# Revit family: 6MLH-NRG
name_source: partatom
category: Mechanical Equipment
revit_build: Autodesk Revit 2017 (Build: 20190508_0315(x64)
units: mm (PartAtom-declared; Revit-internal decimal feet)

## family parameters
Always vertical = Yes
Cut with Voids When Loaded = No
OmniClass Number = 23.40.40.11.17
OmniClass Title = Refrigerated Cases
Part Type = Normal
Room Calculation Point = No
Round Connector Dimension = Use Radius
Shared = No
Work Plane-Based = Yes

## types (12) — shared parameters
24" Shelf = Yes
BOTTOM ELECTRICAL = Yes
BOTTOM REFRIGERATION PIPING = Yes
Certifications = NSF 7, UL471, CSA
DATE = 04/29/2016
DRAIN PIPING = Yes
Default Elevation = 48"
Description = High Multi-Deck Merchandiser with Synerg-E™
Discharge Air Velocity (FPM) = 260 FPM
EQUIPMENT DESCRIPTION = High Multi-Deck Merchandiser with Synerg-E™
EQUIPMENT MARK = 6MLH-NRG
GLASS = Glass
Height = 88 5/8"
Item Description = High Multi-Deck Merchandiser with Synerg-E™
LF STD END = Yes
Legend Number = 6MLH-NRG
Manufacturer = HILL PHOENIX
Model = 6MLH-NRG
PAINTED METAL UPPER SHELF = PAINTED SHELVES
REFRIGERATION PIPING = COPPER PIPE
RT STD END = Yes
STAINLESS STEEL = GALVANIZED STEEL
Standard Power Amps = 0 A
Superheat Set Point @ Bulb (°F) = 6-8 °F
TOP ELECTRICAL = Yes
TOP REFRIGERATION PIPING = Yes
URL = http://www.hillphoenix.com
Width = 42 3/4"

## per-type parameters (varying)
| type | Application Discipline | BTUH Conventional | BTUH Parallel | DRAIN LINE | Defrosts Per Day | Discharge Air (°F) | ENDS 4 SECTION | Evaporator (°F) | High Efficiency Amps | High Efficiency Watts | High Power (Cornice) Amps | High Power (Cornice) Watts | Length | Length of Cases | Light Length | Lights Per Row | Number of Fans | Standard Power Watts | Timed-Off Defrost Fail-Safe (Min) | Timed-Off Defrost Termination Temp |
| 04' Dairy/Deli/Cut Produce | Fresh Meat | 1915 | 1770 | 24" | 2 | 30 °F | Yes | 27 °F | 1 A | 65 W | 1 A | 65 W | 48" | 48" | 3' | 2 | 3 | 36 W | 30 (min) | 42 °F |
| 06' Dairy/Deli/Cut Produce | Dairy/Deli/Cut Produce | 1756 | 1500 | 36" | 6 | 34 °F | Yes | 25 °F | 1 A | 65 W | 0 A | 30 W | 72" | 72" | 3' | 2 | 3 | 17 W | 45 (min) | 42 °F |
| 08' Dairy/Deli/Cut Produce | Dairy/Deli/Cut Produce | 1756 | 1500 | 48" | 8 | 34 °F | Yes | 25 °F | 1 A | 65 W | 0 A | 43 W | 96" | 96" | 4' | 2 | 3 | 24 W | 45 | 45 °F |
| 12' Dairy/Deli/Cut Produce | Dairy/Deli/Cut Produce | 1756 | 1500 | 72" | 6 | 34 °F | Yes | 25 °F | 1 A | 87 W | 1 A | 65 W | 144" | 144" | 4' | 3 | 4 | 36 W | 45 (min) | 42 °F |
| 04' Bulk Produce/Beverage | Bulk Produce/Beverage | 1545 | 1475 | 24" | 6 | 37 °F | No | 34 °F | 0 A | 43 W | 0 A | 22 W | 48" | 48" | 4' | 1 | 2 | 12 W | 45 (min) | 42 °F |
| 06' Bulk Produce/Beverage | Bulk Produce/Beverage | 1756 | 1500 | 36" | 6 | 34 °F | Yes | 25 °F | 1 A | 65 W | 0 A | 30 W | 72" | 72" | 3' | 2 | 3 | 17 W | 45 (min) | 42 °F |
| 08' Bulk Produce/Beverage | Bulk Produce/Beverage | 1756 | 1500 | 48" | 6 | 34 °F | Yes | 25 °F | 1 A | 65 W | 0 A | 43 W | 96" | 96" | 4' | 2 | 3 | 24 W | 45 (min) | 42 °F |
| 12' Bulk Produce/Beverage | Bulk Produce/Beverage | 1756 | 1500 | 72" | 6 | 34 °F | Yes | 25 °F | 1 A | 87 W | 1 A | 65 W | 144" | 144" | 4' | 3 | 4 | 36 W | 45 (min) | 42 °F |
| 12' | Bulk Produce/Beverage | 1756 | 1500 | 72" | 6 | 34 °F | Yes | 25 °F | 1 A | 87 W | 1 A | 65 W | 144" | 144" | 4' | 3 | 4 | 36 W | 45 (min) | 42 °F |
| 8' | Bulk Produce/Beverage | 1756 | 1500 | 48" | 6 | 34 °F | Yes | 25 °F | 1 A | 65 W | 1 A | 65 W | 96" | 144" | 4' | 2 | 3 | 36 W | 45 (min) | 42 °F |
| 6' | Bulk Produce/Beverage | 1545 | 1475 | 36" | 2 | 37 °F | Yes | 34 °F | 1 A | 65 W | 1 A | 65 W | 72" | 144" | 3' | 2 | 3 | 36 W | 30 (min) | 42 °F |
| 4' | Dairy/Deli/Cut Produce | 1695 | 1585 | 24" | 6 | 31 °F | Yes | 28 °F | 0 A | 43 W | 1 A | 65 W | 48" | 144" | 4' | 1 | 2 | 36 W | 45 (Min) | 42 °F |

## geometry (parser evidence)
native form markers: Blend x16, Sweep x22
no freeform markers — native parametric forms only
